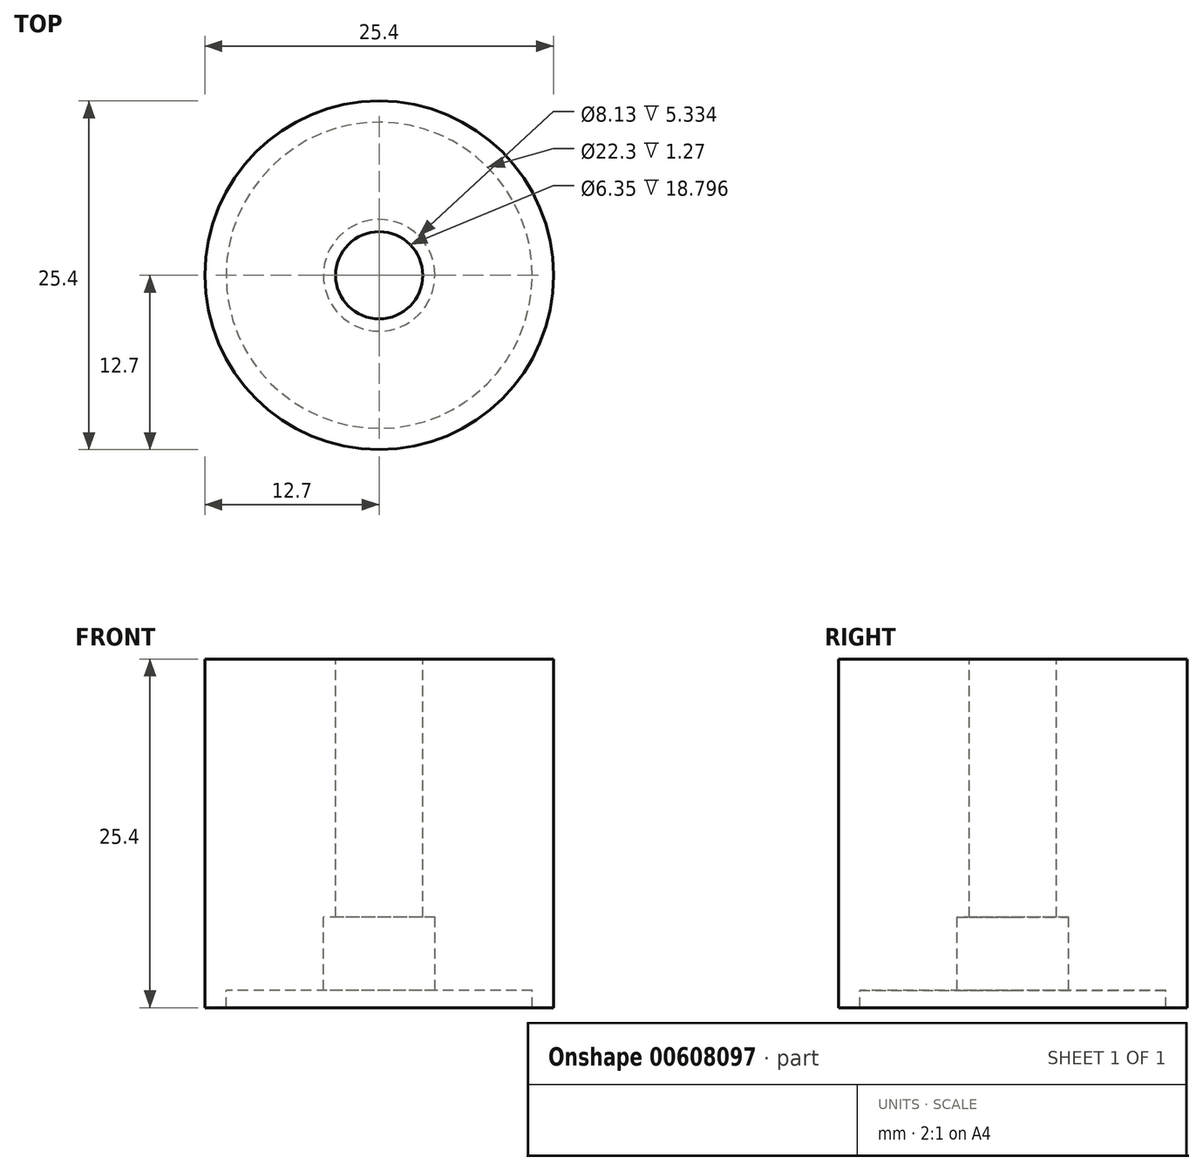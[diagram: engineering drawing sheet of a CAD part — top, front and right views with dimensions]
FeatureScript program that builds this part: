
annotation { "Feature Type Name" : "Feature", "Feature Type Description" : "" }
export const myFeature = defineFeature(function(context is Context, id is Id, definition is map)
    precondition{}
    {
        {
            var Q0;
            Q0=qCreatedBy(makeId("Front.planeOp"),FACE);
            var sketch = newSketch(context, id + "F0", { "sketchPlane" : qUnion([Q0])});
            skLineSegment(sketch, "E0", {"start": v(0, 0) * mm, "end": v(0, -10.67) * mm, "construction": true});
            skLineSegment(sketch, "E1", {"start": v(4.06, 0) * mm, "end": v(11.15, 0) * mm});
            skLineSegment(sketch, "E2", {"start": v(11.15, 0) * mm, "end": v(11.15, -1.27) * mm});
            skLineSegment(sketch, "E3", {"start": v(11.15, -1.27) * mm, "end": v(12.7, -1.27) * mm});
            skLineSegment(sketch, "E4", {"start": v(12.7, -1.27) * mm, "end": v(12.7, 24.13) * mm});
            skLineSegment(sketch, "E5", {"start": v(12.7, 24.13) * mm, "end": v(3.17, 24.13) * mm});
            skLineSegment(sketch, "E6", {"start": v(3.17, 24.13) * mm, "end": v(3.17, 5.33) * mm});
            skLineSegment(sketch, "E7", {"start": v(4.06, 0) * mm, "end": v(4.06, 5.33) * mm});
            skLineSegment(sketch, "E8", {"start": v(4.06, 5.33) * mm, "end": v(3.17, 5.33) * mm});
            skPoint(sketch, "E9.orphan", {"position": v(3.17, 0) * mm});
            skSolve(sketch);
        }
        {
            var Q0;
            Q0 = qSketchRegion(id + "F0", true);
            var Q1;
            Q1=sQuery(id+"F0.wireOp",EDGE,"E0");
            revolve(context, id + "F1", {"entities" : qUnion([Q0]), "axis" : qUnion([Q1]), "revolveType" : RevolveType.FULL});
        }
    });
